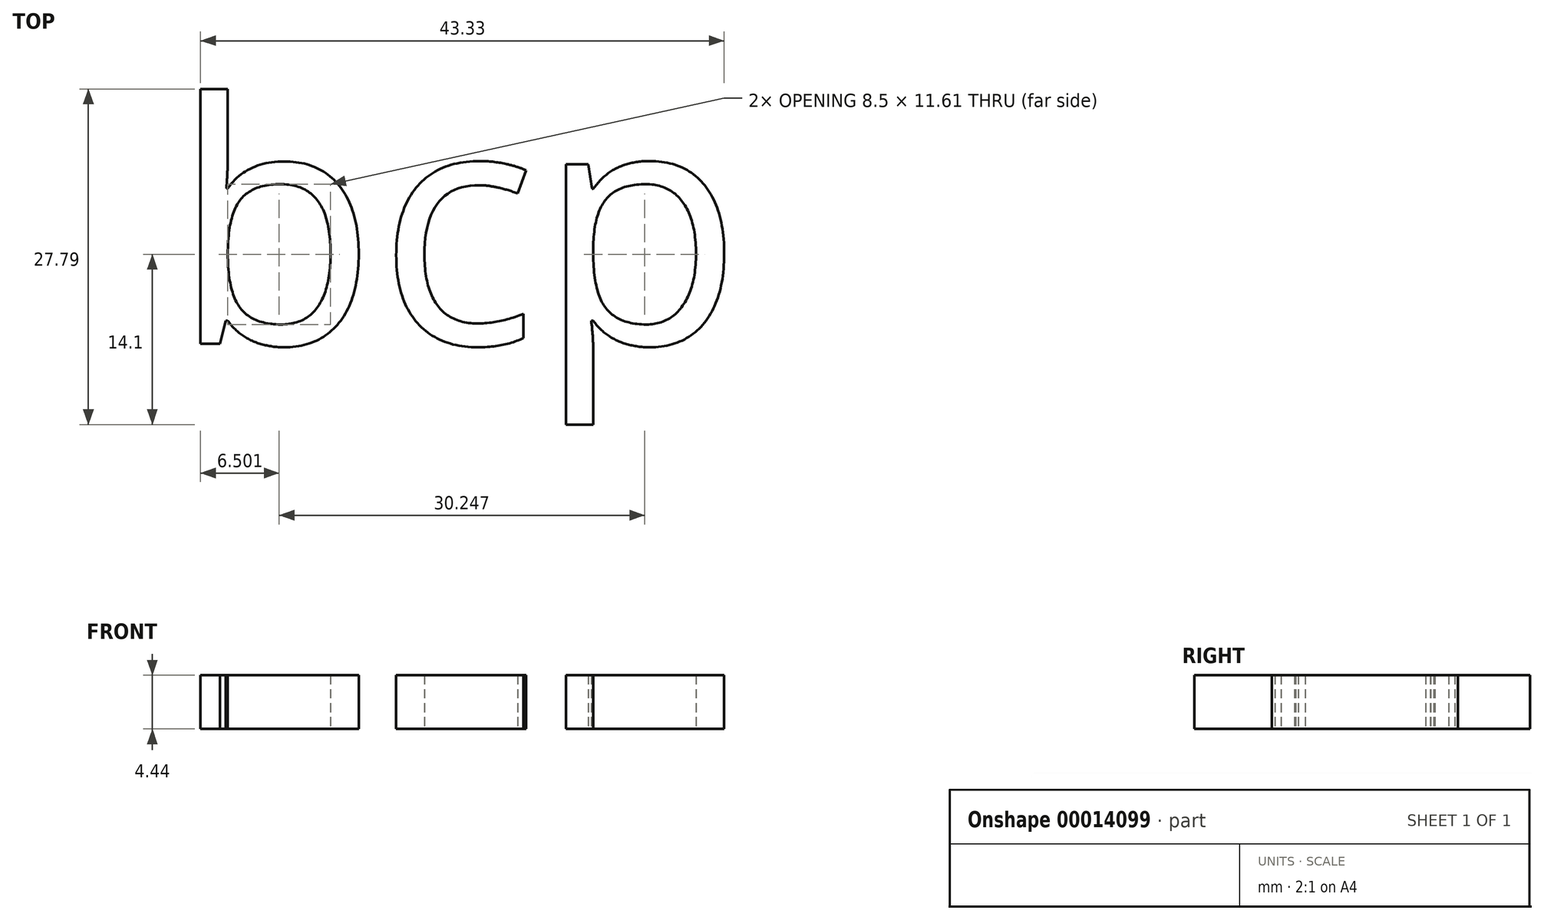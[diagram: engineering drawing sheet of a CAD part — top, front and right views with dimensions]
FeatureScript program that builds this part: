
annotation { "Feature Type Name" : "Feature", "Feature Type Description" : "" }
export const myFeature = defineFeature(function(context is Context, id is Id, definition is map)
    precondition{}
    {
        {
            var Q0;
            Q0=qCreatedBy(makeId("Top.planeOp"),FACE);
            var sketch = newSketch(context, id + "F0", { "sketchPlane" : qUnion([Q0])});
            skText(sketch, "E0", { "text": "bcp", "fontName": "OpenSans-Regular.ttf"});
            const initialGuessF0  = {"E0": [0, -0.02, 1, 0, 0.02]};
            skSetInitialGuess(sketch, initialGuessF0);
            skSolve(sketch);
        }
        {
            var Q0;
            Q0 = qSketchRegion(id + "F0", true);
            extrude(context, id + "F1", {"entities" : qUnion([Q0]), "depth" : 4.44 * mm});
        }
    });
